# Revit family: Tube_de_chasse_63-50mmxL53cm
name_source: partatom
category: Plumbing Fixtures
units: mm (PartAtom-declared; Revit-internal decimal feet)

## family parameters
Always vertical = Yes
Cut with Voids When Loaded = No
OmniClass Number = 23.45.00.00
OmniClass Title = Sanitary, Laundry, and Cleaning Equipment
Part Type = Normal
Room Calculation Point = No
Round Connector Dimension = Use Diameter
Shared = No
Work Plane-Based = No

## types (1)
- Tube_de_chasse_63-50mmxL53cm
    BIM object developer = www.concepsysbim.com
    Description = Tube permettant l’installation désaxée des réservoirs Césame CE70 - CE71 - CE72.
    Manufacturer = REGIPLAST
    Model = Tube de chasse Ø63-50mmxL53cm
    Regiplast_Matériel = <By Category>
    TUBE_Description technique = https://professionnels.regiplast.fr
    TUBE_Dimensions = Ø63-50mmx530mm
    TUBE_Désaxement latéral possible = 0 à 520 mm
    TUBE_Marque = REGIPLAST
    TUBE_Matériel = PP
    TUBE_Modèle = Tube de chasse Ø63-50mmxL53cm
    TUBE_Notice d'installation = https://professionnels.regiplast.fr
    TUBE_Produit = Tube de chasse
    TUBE_Recoupe possible = 200 mm  [stored 0.656168 ft]
    TUBE_Référence du modèle = TS800
    TUBE_Site internet/Page web = https://www.regiplast.fr
    TUBE_Type/fonctionnement = Tube permettant l’installation désaxée des réservoirs Césame CE70 - CE71 - CE72.
    TUBE_URL des données du produit = https://professionnels.regiplast.fr
    URL = https://professionnels.regiplast.fr

note: [stored X ft] marks values corroborated as IEEE doubles in the binary element streams (Revit-internal decimal feet)

## geometry (parser evidence)
native form markers: Sweep x7
no freeform markers — native parametric forms only
